# Revit family: Furniture-Lighted_Mirror-KOHLER-Forefront-K-23266IN_1
name_source: partatom
category: Lighting Fixtures
units: mm (PartAtom-declared; Revit-internal decimal feet)

## family parameters
Cut with Voids When Loaded = No
Host = Face
Light Source = Yes
Maintain Annotation Orientation = No
OmniClass Number = 23.21.37.13.15
OmniClass Title = Mirrors
Part Type = Normal
Room Calculation Point = No
Round Connector Dimension = Use Diameter
Shared = No

## types (1)
- NA-Anodized Aluminum
    ADA Compliant = No
    Apparent Load = 250 VA
    Assembly Code = D5020200
    Color Filter = 16777215
    Date Modified = 05/05/2022
    Default Elevation = 60"
    Description = Time Mirror 900mm
    Dimming Lamp Color Temperature Shift = Incandescent Lamp Curve
    Electrical Connector = Yes
    Electrical Note = One Dedicated Circuit Required
    Emit from Line Length = 24"
    Finish = Kohler-Metal-NA-Anodized_Aluminum
    Height = 25 9/16"
    Lamp = LED
    Length = 1 3/16"
    Light Source Symbol Size = 6"
    Manufacturer = Kohler Co.
    Master Format 2014 = 41 53 13
    Master Format 2014 Name = Storage Cabinets
    Material = Anodized Aluminum Construction
    Model = K-23266IN-NA
    Product Name = Forefront
    Type = 1
    URL = https://www.kohler.co.in
    Voltage = 12 V
    WaterSense Certified = No
    Wattage Comments = 170-250VAC
    Width = 35 7/16"

## geometry (parser evidence)
native form markers: Sweep x5
no freeform markers — native parametric forms only
